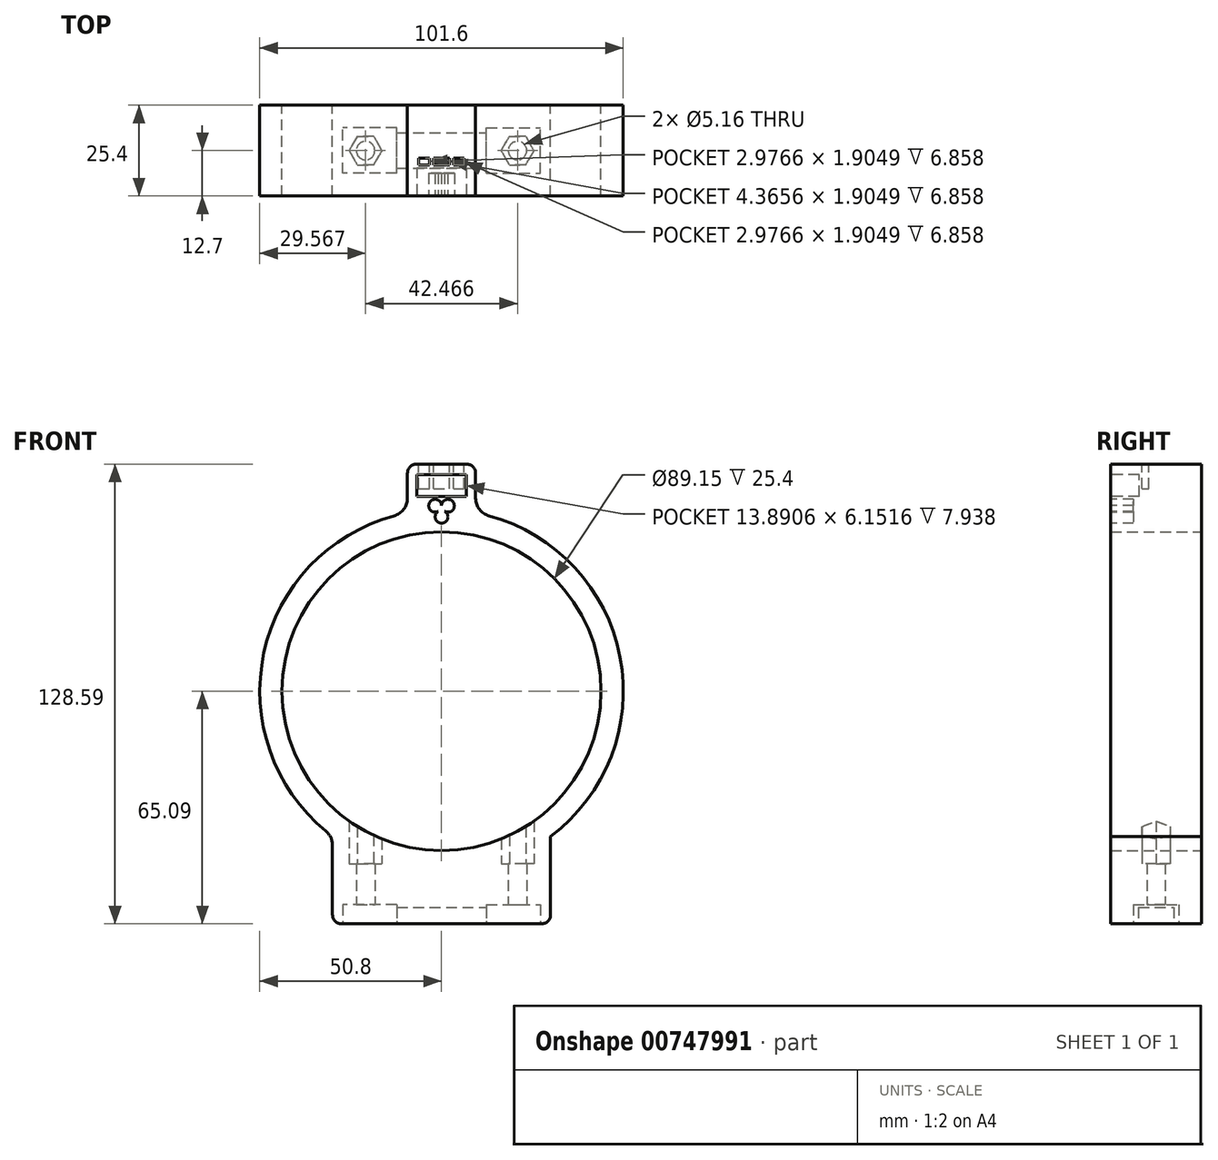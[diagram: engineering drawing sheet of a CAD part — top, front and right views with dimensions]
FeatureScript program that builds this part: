
annotation { "Feature Type Name" : "Feature", "Feature Type Description" : "" }
export const myFeature = defineFeature(function(context is Context, id is Id, definition is map)
    precondition{}
    {
        {
            var Q0;
            Q0=qCreatedBy(makeId("Front.planeOp"),FACE);
            var sketch = newSketch(context, id + "F0", { "sketchPlane" : qUnion([Q0])});
            skCircle(sketch, "E0", {"center": v(0, 0) * mm, "radius": 44.58 * mm});
            skCircle(sketch, "E1", {"center": v(0, 0) * mm, "radius": 50.8 * mm});
            skLineSegment(sketch, "E2.bottom", {"start": v(-9.52, 0) * mm, "end": v(9.53, 0) * mm});
            skLineSegment(sketch, "E2.top", {"start": v(-9.53, 63.5) * mm, "end": v(9.52, 63.5) * mm});
            skLineSegment(sketch, "E2.left", {"start": v(-9.52, 0) * mm, "end": v(-9.53, 63.5) * mm});
            skLineSegment(sketch, "E2.right", {"start": v(9.53, 0) * mm, "end": v(9.52, 63.5) * mm});
            skSolve(sketch);
        }
        {
            var Q0;
            {var subQ0=sQuery(id+"F0.wireOp",EDGE,"E2.left");var subQ1=sQuery(id+"F0.wireOp",EDGE,"E0");var subQ2=makeQuery(id+"F0.imprint","INTERSECT",VERTEX,{"derivedFrom":[subQ1,subQ0]});Q0=makeQuery(id+"F0.imprint","IMPRINT",FACE,{"disambiguationData":[TD([[makeQuery(id+"F0.imprint","IMPRINT",EDGE,{"disambiguationData":[TD([[subQ2,-1.0]])],"derivedFrom":subQ1}),-1.0]])]});}
            var Q1;
            {var subQ0=sQuery(id+"F0.wireOp",EDGE,"E2.left");var subQ1=sQuery(id+"F0.wireOp",EDGE,"E0");var subQ2=makeQuery(id+"F0.imprint","INTERSECT",VERTEX,{"derivedFrom":[subQ1,subQ0]});Q1=makeQuery(id+"F0.imprint","IMPRINT",FACE,{"disambiguationData":[TD([[makeQuery(id+"F0.imprint","IMPRINT",EDGE,{"disambiguationData":[TD([[subQ2,1.0]])],"derivedFrom":subQ1}),-1.0]])]});}
            var Q2;
            {var subQ5=sQuery(id+"F0.wireOp",EDGE,"E2.top");Q2=makeQuery(id+"F0.imprint","IMPRINT",FACE,{"disambiguationData":[TD([[makeQuery(id+"F0.imprint","IMPRINT",EDGE,{"derivedFrom":subQ5}),-1.0]])]});}
            extrude(context, id + "F1", {"entities" : qUnion([Q0, Q1, Q2]), "depth" : 25.4 * mm, "offsetDistance" : 25.4 * mm});
        }
        {
            var Q0;
            Q0=makeQuery(id+"F1.opExtrude","CAP_FACE",FACE,{"disambiguationData":[OSD([sQuery(id+"F0.wireOp",EDGE,"E0"),sQuery(id+"F0.wireOp",EDGE,"E1"),sQuery(id+"F0.wireOp",EDGE,"E2.top"),sQuery(id+"F0.wireOp",EDGE,"E2.left"),sQuery(id+"F0.wireOp",EDGE,"E2.right")])],"isStart":false});
            var sketch = newSketch(context, id + "F2", { "sketchPlane" : qUnion([Q0])});
            skCircle(sketch, "E3", {"center": v(1.79, 51.87) * mm, "radius": 1.79 * mm});
            skCircle(sketch, "E4.MirrorC", {"center": v(-1.79, 51.87) * mm, "radius": 1.79 * mm});
            skCircle(sketch, "E5", {"center": v(0, 48.78) * mm, "radius": 1.79 * mm});
            skSolve(sketch);
        }
        {
            var Q0;
            Q0 = qSketchRegion(id + "F2", true);
            extrude(context, id + "F3", {"entities" : qUnion([Q0]), "operationType" : NewBodyOperationType.REMOVE, "oppositeDirection" : true, "depth" : 6.35 * mm, "offsetDistance" : 25.4 * mm});
        }
        {
            var Q0;
            Q0=makeQuery(id+"F1.opExtrude","CAP_FACE",FACE,{"disambiguationData":[OSD([sQuery(id+"F0.wireOp",EDGE,"E0"),sQuery(id+"F0.wireOp",EDGE,"E1"),sQuery(id+"F0.wireOp",EDGE,"E2.top"),sQuery(id+"F0.wireOp",EDGE,"E2.left"),sQuery(id+"F0.wireOp",EDGE,"E2.right")])],"isStart":false});
            var sketch = newSketch(context, id + "F4", { "sketchPlane" : qUnion([Q0])});
            skLineSegment(sketch, "E6.bottom", {"start": v(-6.95, 54.47) * mm, "end": v(6.95, 54.47) * mm});
            skLineSegment(sketch, "E6.top", {"start": v(-6.95, 60.62) * mm, "end": v(6.95, 60.62) * mm});
            skLineSegment(sketch, "E6.left", {"start": v(-6.95, 54.47) * mm, "end": v(-6.95, 60.62) * mm});
            skLineSegment(sketch, "E6.right", {"start": v(6.95, 54.47) * mm, "end": v(6.95, 60.62) * mm});
            skSolve(sketch);
        }
        {
            var Q0;
            Q0=makeQuery(id+"F4.imprint","IMPRINT",FACE,{"disambiguationData":[TD([[makeQuery(id+"F4.imprint","IMPRINT",EDGE,{"derivedFrom":sQuery(id+"F4.wireOp",EDGE,"E6.bottom")}),1.0]])]});
            extrude(context, id + "F5", {"entities" : qUnion([Q0]), "operationType" : NewBodyOperationType.REMOVE, "oppositeDirection" : true, "depth" : 7.94 * mm, "offsetDistance" : 25.4 * mm});
        }
        {
            var Q0;
            Q0=makeQuery(id+"F1.opExtrude","SWEPT_FACE",FACE,{"disambiguationData":[OSD([sQuery(id+"F0.wireOp",EDGE,"E2.top")])]});
            var sketch = newSketch(context, id + "F6", { "sketchPlane" : qUnion([Q0])});
            skLineSegment(sketch, "E7", {"start": v(-12.7, -16.67) * mm, "end": v(17.23, -16.67) * mm, "construction": true});
            skLineSegment(sketch, "E8.bottom", {"start": v(-6.35, -16.67) * mm, "end": v(6.35, -16.67) * mm});
            skLineSegment(sketch, "E8.top", {"start": v(-6.35, -14.76) * mm, "end": v(6.35, -14.76) * mm});
            skLineSegment(sketch, "E8.left", {"start": v(-6.35, -16.67) * mm, "end": v(-6.35, -14.76) * mm});
            skLineSegment(sketch, "E8.right", {"start": v(6.35, -16.67) * mm, "end": v(6.35, -14.76) * mm});
            skSolve(sketch);
        }
        {
            var Q0;
            Q0 = qSketchRegion(id + "F6", true);
            extrude(context, id + "F7", {"entities" : qUnion([Q0]), "operationType" : NewBodyOperationType.REMOVE, "oppositeDirection" : true, "depth" : 6.86 * mm, "offsetDistance" : 25.4 * mm});
        }
        {
            var Q0;
            Q0=makeQuery(id+"F1.opExtrude","SWEPT_FACE",FACE,{"disambiguationData":[OSD([sQuery(id+"F0.wireOp",EDGE,"E2.top")])]});
            var sketch = newSketch(context, id + "F8", { "sketchPlane" : qUnion([Q0])});
            skLineSegment(sketch, "E9.bottom", {"start": v(3.37, -16.67) * mm, "end": v(2.18, -16.67) * mm});
            skLineSegment(sketch, "E9.top", {"start": v(3.37, -14.76) * mm, "end": v(2.18, -14.76) * mm});
            skLineSegment(sketch, "E9.left", {"start": v(3.37, -16.67) * mm, "end": v(3.37, -14.76) * mm});
            skLineSegment(sketch, "E9.right", {"start": v(2.18, -16.67) * mm, "end": v(2.18, -14.76) * mm});
            skLineSegment(sketch, "E10.bottom", {"start": v(-2.18, -16.67) * mm, "end": v(-3.37, -16.67) * mm});
            skLineSegment(sketch, "E10.top", {"start": v(-2.18, -14.76) * mm, "end": v(-3.37, -14.76) * mm});
            skLineSegment(sketch, "E10.left", {"start": v(-2.18, -16.67) * mm, "end": v(-2.18, -14.76) * mm});
            skLineSegment(sketch, "E10.right", {"start": v(-3.37, -16.67) * mm, "end": v(-3.37, -14.76) * mm});
            skSolve(sketch);
        }
        {
            var Q0;
            Q0 = qSketchRegion(id + "F8", true);
            extrude(context, id + "F9", {"entities" : qUnion([Q0]), "operationType" : NewBodyOperationType.ADD, "oppositeDirection" : true, "depth" : 12.7 * mm, "offsetDistance" : 25.4 * mm});
        }
        {
            var Q0;
            Q0=qCreatedBy(makeId("Front.planeOp"),FACE);
            var sketch = newSketch(context, id + "F10", { "sketchPlane" : qUnion([Q0])});
            skLineSegment(sketch, "E11.bottom", {"start": v(30.48, -65.09) * mm, "end": v(-30.48, -65.09) * mm});
            skLineSegment(sketch, "E12", {"start": v(-30.48, -65.09) * mm, "end": v(-30.48, -40.64) * mm});
            skLineSegment(sketch, "E13", {"start": v(30.48, -65.09) * mm, "end": v(30.48, -40.64) * mm});
            skArc(sketch, "E14", {"start": v(-30.48, -40.64) * mm, "mid": v(0, -50.8) * mm, "end": v(30.48, -40.64) * mm});
            skLineSegment(sketch, "E15", {"start": v(-46.13, -44.45) * mm, "end": v(49.26, -44.45) * mm, "construction": true});
            skLineSegment(sketch, "E16", {"start": v(0, -44.45) * mm, "end": v(0, -75.8) * mm, "construction": true});
            skSolve(sketch);
        }
        {
            var Q0;
            Q0 = qSketchRegion(id + "F10", true);
            extrude(context, id + "F11", {"entities" : qUnion([Q0]), "operationType" : NewBodyOperationType.ADD, "depth" : 25.4 * mm, "offsetDistance" : 25.4 * mm});
        }
        {
            var Q0;
            Q0=makeQuery(id+"F11.opExtrude","SWEPT_FACE",FACE,{"disambiguationData":[OSD([sQuery(id+"F10.wireOp",EDGE,"E11.bottom")])]});
            var sketch = newSketch(context, id + "F12", { "sketchPlane" : qUnion([Q0])});
            skLineSegment(sketch, "E17.bottom", {"start": v(12.5, 19.05) * mm, "end": v(27.58, 19.05) * mm});
            skLineSegment(sketch, "E17.top", {"start": v(12.5, 6.35) * mm, "end": v(27.58, 6.35) * mm});
            skLineSegment(sketch, "E17.left", {"start": v(12.5, 19.05) * mm, "end": v(12.5, 6.35) * mm});
            skLineSegment(sketch, "E17.right", {"start": v(27.58, 19.05) * mm, "end": v(27.58, 6.35) * mm});
            skLineSegment(sketch, "E18.MirrorCS", {"start": v(-12.5, 19.05) * mm, "end": v(-27.58, 19.05) * mm});
            skLineSegment(sketch, "E19.MirrorCS", {"start": v(-12.5, 19.05) * mm, "end": v(-12.5, 6.35) * mm});
            skLineSegment(sketch, "E20.MirrorCS", {"start": v(-12.5, 6.35) * mm, "end": v(-27.58, 6.35) * mm});
            skLineSegment(sketch, "E21.MirrorCS", {"start": v(-27.58, 19.05) * mm, "end": v(-27.58, 6.35) * mm});
            skPoint(sketch, "E22.centerSnap0", {"position": v(12.5, 12.7) * mm});
            skSolve(sketch);
        }
        {
            var Q0;
            Q0 = qSketchRegion(id + "F12", true);
            extrude(context, id + "F13", {"entities" : qUnion([Q0]), "operationType" : NewBodyOperationType.REMOVE, "oppositeDirection" : true, "depth" : 5.36 * mm, "offsetDistance" : 25.4 * mm});
        }
        {
            var Q0;
            Q0=makeQuery(id+"F13.boolean.opBoolean","COPY",FACE,{"derivedFrom":makeQuery(id+"F13.opExtrude","CAP_FACE",FACE,{"disambiguationData":[OSD([sQuery(id+"F12.wireOp",EDGE,"E17.bottom"),sQuery(id+"F12.wireOp",EDGE,"E17.top"),sQuery(id+"F12.wireOp",EDGE,"E17.left"),sQuery(id+"F12.wireOp",EDGE,"E17.right")])],"isStart":false})});
            var sketch = newSketch(context, id + "F14", { "sketchPlane" : qUnion([Q0])});
            skCircle(sketch, "E23", {"center": v(21.23, 12.7) * mm, "radius": 2.58 * mm});
            skPoint(sketch, "E23.centerSnap0", {"position": v(12.5, 12.7) * mm});
            skCircle(sketch, "E24.MirrorC", {"center": v(-21.23, 12.7) * mm, "radius": 2.58 * mm});
            skSolve(sketch);
        }
        {
            var Q0;
            Q0 = qSketchRegion(id + "F14", true);
            extrude(context, id + "F15", {"entities" : qUnion([Q0]), "operationType" : NewBodyOperationType.REMOVE, "oppositeDirection" : true, "depth" : 25.4 * mm, "offsetDistance" : 25.4 * mm});
        }
        {
            var Q0;
            Q0=qCreatedBy(makeId("Top.planeOp"),FACE);
            cPlane(context, id + "F16", {"entities" : qUnion([Q0]), "cplaneType" : CPlaneType.OFFSET, "offset" : 48.26 * mm, "oppositeDirection" : true, "width" : 152.4 * mm, "height" : 152.4 * mm});
        }
        {
            var Q0;
            Q0=qCreatedBy(id+"F16.planeOp",FACE);
            var sketch = newSketch(context, id + "F17", { "sketchPlane" : qUnion([Q0])});
            skCircle(sketch, "E25.cCircle", {"center": v(21.23, -12.7) * mm, "radius": 3.97 * mm, "construction": true});
            skLineSegment(sketch, "E25.0", {"start": v(23.52, -16.67) * mm, "end": v(18.94, -16.67) * mm});
            skLineSegment(sketch, "E25.1", {"start": v(18.94, -16.67) * mm, "end": v(16.65, -12.7) * mm});
            skLineSegment(sketch, "E25.2", {"start": v(16.65, -12.7) * mm, "end": v(18.94, -8.73) * mm});
            skLineSegment(sketch, "E25.3", {"start": v(18.94, -8.73) * mm, "end": v(23.52, -8.73) * mm});
            skLineSegment(sketch, "E25.4", {"start": v(23.52, -8.73) * mm, "end": v(25.82, -12.7) * mm});
            skLineSegment(sketch, "E25.5", {"start": v(25.82, -12.7) * mm, "end": v(23.52, -16.67) * mm});
            skPoint(sketch, "E25.0.midPoint", {"position": v(21.23, -16.67) * mm});
            skLineSegment(sketch, "E26.MirrorCS", {"start": v(-23.52, -16.67) * mm, "end": v(-18.94, -16.67) * mm});
            skLineSegment(sketch, "E27.MirrorCS", {"start": v(-18.94, -16.67) * mm, "end": v(-16.65, -12.7) * mm});
            skLineSegment(sketch, "E28.MirrorCS", {"start": v(-16.65, -12.7) * mm, "end": v(-18.94, -8.73) * mm});
            skLineSegment(sketch, "E29.MirrorCS", {"start": v(-18.94, -8.73) * mm, "end": v(-23.52, -8.73) * mm});
            skLineSegment(sketch, "E30.MirrorCS", {"start": v(-23.52, -8.73) * mm, "end": v(-25.82, -12.7) * mm});
            skLineSegment(sketch, "E31.MirrorCS", {"start": v(-25.82, -12.7) * mm, "end": v(-23.52, -16.67) * mm});
            skSolve(sketch);
        }
        {
            var Q0;
            Q0 = qSketchRegion(id + "F17", true);
            extrude(context, id + "F18", {"entities" : qUnion([Q0]), "operationType" : NewBodyOperationType.REMOVE, "depth" : 25.4 * mm, "offsetDistance" : 25.4 * mm});
        }
        {
            var Q0;
            Q0=makeQuery(id+"F11.opExtrude","SWEPT_FACE",FACE,{"disambiguationData":[OSD([sQuery(id+"F10.wireOp",EDGE,"E11.bottom")])]});
            var sketch = newSketch(context, id + "F19", { "sketchPlane" : qUnion([Q0])});
            skLineSegment(sketch, "E32.bottom", {"start": v(-12.5, 17.66) * mm, "end": v(12.5, 17.66) * mm});
            skLineSegment(sketch, "E32.top", {"start": v(-12.5, 7.74) * mm, "end": v(12.5, 7.74) * mm});
            skLineSegment(sketch, "E32.left", {"start": v(-12.5, 17.66) * mm, "end": v(-12.5, 7.74) * mm});
            skLineSegment(sketch, "E32.right", {"start": v(12.5, 17.66) * mm, "end": v(12.5, 7.74) * mm});
            skLineSegment(sketch, "E33", {"start": v(-12.5, 12.7) * mm, "end": v(12.5, 12.7) * mm, "construction": true});
            skSolve(sketch);
        }
        {
            var Q0;
            Q0=makeQuery(id+"F19.imprint","IMPRINT",FACE,{"disambiguationData":[TD([[makeQuery(id+"F19.imprint","IMPRINT",EDGE,{"derivedFrom":sQuery(id+"F19.wireOp",EDGE,"E32.bottom")}),-1.0]])]});
            extrude(context, id + "F20", {"entities" : qUnion([Q0]), "operationType" : NewBodyOperationType.REMOVE, "oppositeDirection" : true, "depth" : 4.56 * mm, "offsetDistance" : 25.4 * mm});
        }
        {
            var Q0;
            Q0=makeQuery(id+"F11.opExtrude","SWEPT_EDGE",EDGE,{"disambiguationData":[OSD([sQuery(id+"F10.wireOp",EDGE,"E11.bottom"),sQuery(id+"F10.wireOp",EDGE,"E12")])]});
            var Q1;
            Q1=makeQuery(id+"F11.opExtrude","SWEPT_EDGE",EDGE,{"disambiguationData":[OSD([sQuery(id+"F10.wireOp",EDGE,"E11.bottom"),sQuery(id+"F10.wireOp",EDGE,"E13")])]});
            fillet(context, id + "F21", {"entities" : qUnion([Q0, Q1]), "radius" : 2.54 * mm, "tangentPropagation" : true, "allowEdgeOverflow" : false});
        }
        {
            var Q0;
            Q0=makeQuery(id+"F1.opExtrude","SWEPT_EDGE",EDGE,{"disambiguationData":[OSD([sQuery(id+"F0.wireOp",EDGE,"E2.top"),sQuery(id+"F0.wireOp",EDGE,"E2.left")])]});
            var Q1;
            Q1=makeQuery(id+"F1.opExtrude","SWEPT_EDGE",EDGE,{"disambiguationData":[OSD([sQuery(id+"F0.wireOp",EDGE,"E2.top"),sQuery(id+"F0.wireOp",EDGE,"E2.right")])]});
            fillet(context, id + "F22", {"entities" : qUnion([Q0, Q1]), "radius" : 2.54 * mm, "tangentPropagation" : true, "allowEdgeOverflow" : false});
        }
        {
            var Q0;
            Q0=makeQuery(id+"F1.opExtrude","SWEPT_EDGE",EDGE,{"disambiguationData":[OSD([sQuery(id+"F0.wireOp",EDGE,"E1"),sQuery(id+"F0.wireOp",EDGE,"E2.right")])]});
            var Q1;
            Q1=makeQuery(id+"F1.opExtrude","SWEPT_EDGE",EDGE,{"disambiguationData":[OSD([sQuery(id+"F0.wireOp",EDGE,"E1"),sQuery(id+"F0.wireOp",EDGE,"E2.left")])]});
            var Q2;
            Q2=makeQuery(id+"F11.opExtrude","SWEPT_EDGE",EDGE,{"disambiguationData":[OSD([sQuery(id+"F10.wireOp",EDGE,"E13"),sQuery(id+"F10.wireOp",EDGE,"E14")])]});
            var Q3;
            Q3=makeQuery(id+"F11.opExtrude","SWEPT_EDGE",EDGE,{"disambiguationData":[OSD([sQuery(id+"F10.wireOp",EDGE,"E12"),sQuery(id+"F10.wireOp",EDGE,"E14")])]});
            fillet(context, id + "F23", {"entities" : qUnion([Q0, Q1, Q2, Q3]), "radius" : 5.08 * mm, "tangentPropagation" : true, "allowEdgeOverflow" : false});
        }
    });
